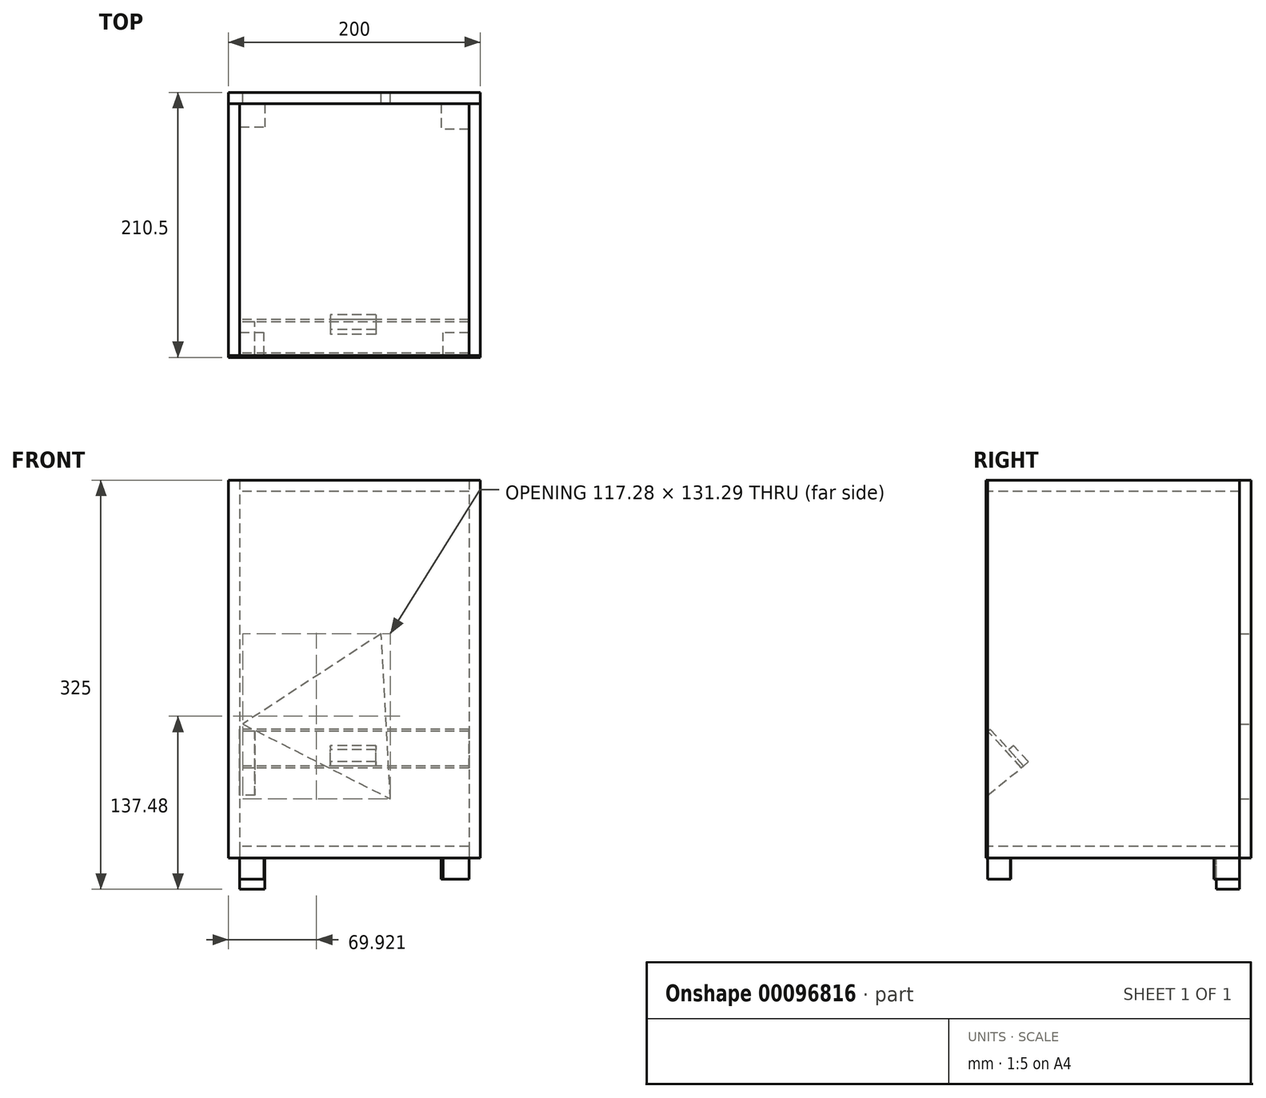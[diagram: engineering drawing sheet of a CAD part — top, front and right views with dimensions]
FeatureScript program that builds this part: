
annotation { "Feature Type Name" : "Feature", "Feature Type Description" : "" }
export const myFeature = defineFeature(function(context is Context, id is Id, definition is map)
    precondition{}
    {
        {
            var Q0;
            Q0=qCreatedBy(makeId("Front.planeOp"),FACE);
            var sketch = newSketch(context, id + "F0", { "sketchPlane" : qUnion([Q0])});
            skLineSegment(sketch, "E0.bottom", {"start": v(0, 0) * mm, "end": v(200, 0) * mm});
            skLineSegment(sketch, "E0.top", {"start": v(0, 300) * mm, "end": v(200, 300) * mm});
            skLineSegment(sketch, "E0.left", {"start": v(0, 0) * mm, "end": v(0, 300) * mm});
            skLineSegment(sketch, "E0.right", {"start": v(200, 0) * mm, "end": v(200, 300) * mm});
            skSolve(sketch);
        }
        {
            var Q0;
            Q0=makeQuery(id+"F0.imprint","IMPRINT",FACE,{"disambiguationData":[TD([[makeQuery(id+"F0.imprint","IMPRINT",EDGE,{"derivedFrom":sQuery(id+"F0.wireOp",EDGE,"E0.bottom")}),1.0]])]});
            extrude(context, id + "F1", {"entities" : qUnion([Q0]), "depth" : 1.5 * mm});
        }
        {
            var Q0;
            Q0=makeQuery(id+"F1.opExtrude","CAP_FACE",FACE,{"disambiguationData":[OSD([sQuery(id+"F0.wireOp",EDGE,"E0.bottom"),sQuery(id+"F0.wireOp",EDGE,"E0.top"),sQuery(id+"F0.wireOp",EDGE,"E0.left"),sQuery(id+"F0.wireOp",EDGE,"E0.right")])],"isStart":true});
            var sketch = newSketch(context, id + "F2", { "sketchPlane" : qUnion([Q0])});
            skLineSegment(sketch, "E1.bottom", {"start": v(0, 300) * mm, "end": v(-9, 300) * mm});
            skLineSegment(sketch, "E1.top", {"start": v(0, 0) * mm, "end": v(-9, 0) * mm});
            skLineSegment(sketch, "E1.left", {"start": v(0, 300) * mm, "end": v(0, 0) * mm});
            skLineSegment(sketch, "E1.right", {"start": v(-9, 300) * mm, "end": v(-9, 0) * mm});
            skSolve(sketch);
        }
        {
            var Q0;
            Q0 = qSketchRegion(id + "F2", true);
            extrude(context, id + "F3", {"entities" : qUnion([Q0]), "depth" : 200 * mm});
        }
        {
            var Q0;
            Q0=makeQuery(id+"F3.opExtrude","SWEPT_FACE",FACE,{"disambiguationData":[OSD([sQuery(id+"F2.wireOp",EDGE,"E1.right")])]});
            var sketch = newSketch(context, id + "F4", { "sketchPlane" : qUnion([Q0])});
            skLineSegment(sketch, "E2", {"start": v(0, 100.67) * mm, "end": v(0, 49.66) * mm});
            skLineSegment(sketch, "E3", {"start": v(0, 49.66) * mm, "end": v(26.79, 71.46) * mm});
            skLineSegment(sketch, "E4", {"start": v(26.79, 71.46) * mm, "end": v(0, 100.67) * mm});
            skSolve(sketch);
        }
        {
            var Q0;
            Q0 = qSketchRegion(id + "F4", true);
            extrude(context, id + "F5", {"entities" : qUnion([Q0]), "depth" : 12 * mm});
        }
        {
            var Q0;
            Q0=makeQuery(id+"F3.opExtrude","SWEPT_FACE",FACE,{"disambiguationData":[OSD([sQuery(id+"F2.wireOp",EDGE,"E1.right")])]});
            var sketch = newSketch(context, id + "F6", { "sketchPlane" : qUnion([Q0])});
            skLineSegment(sketch, "E5", {"start": v(26.7, 71.38) * mm, "end": v(0, 100.68) * mm});
            skLineSegment(sketch, "E6", {"start": v(0, 100.68) * mm, "end": v(1.87, 102.28) * mm});
            skLineSegment(sketch, "E7", {"start": v(1.87, 102.28) * mm, "end": v(28.57, 72.98) * mm});
            skLineSegment(sketch, "E8", {"start": v(28.57, 72.98) * mm, "end": v(26.7, 71.38) * mm});
            skSolve(sketch);
        }
        {
            var Q0;
            Q0 = qSketchRegion(id + "F6", true);
            extrude(context, id + "F7", {"entities" : qUnion([Q0]), "depth" : 182 * mm});
        }
        {
            var Q0;
            Q0=makeQuery(id+"F7.opExtrude","SWEPT_FACE",FACE,{"disambiguationData":[OSD([sQuery(id+"F6.wireOp",EDGE,"E7")])]});
            var sketch = newSketch(context, id + "F8", { "sketchPlane" : qUnion([Q0])});
            skLineSegment(sketch, "E9.bottom", {"start": v(-117.15, 34.7) * mm, "end": v(-80.98, 34.7) * mm});
            skLineSegment(sketch, "E9.top", {"start": v(-117.15, 52.16) * mm, "end": v(-80.98, 52.16) * mm});
            skLineSegment(sketch, "E9.left", {"start": v(-117.15, 34.7) * mm, "end": v(-117.15, 52.16) * mm});
            skLineSegment(sketch, "E9.right", {"start": v(-80.98, 34.7) * mm, "end": v(-80.98, 52.16) * mm});
            skSolve(sketch);
        }
        {
            var Q0;
            Q0 = qSketchRegion(id + "F8", true);
            extrude(context, id + "F9", {"entities" : qUnion([Q0]), "depth" : 5 * mm});
        }
        {
            var Q0;
            Q0=makeQuery(id+"F3.opExtrude","SWEPT_FACE",FACE,{"disambiguationData":[OSD([sQuery(id+"F2.wireOp",EDGE,"E1.right")])]});
            var sketch = newSketch(context, id + "F10", { "sketchPlane" : qUnion([Q0])});
            skLineSegment(sketch, "E10.bottom", {"start": v(200, 300) * mm, "end": v(0, 300) * mm});
            skLineSegment(sketch, "E10.top", {"start": v(200, 291) * mm, "end": v(0, 291) * mm});
            skLineSegment(sketch, "E10.left", {"start": v(200, 300) * mm, "end": v(200, 291) * mm});
            skLineSegment(sketch, "E10.right", {"start": v(0, 300) * mm, "end": v(0, 291) * mm});
            skSolve(sketch);
        }
        {
            var Q0;
            Q0 = qSketchRegion(id + "F10", true);
            extrude(context, id + "F11", {"entities" : qUnion([Q0]), "depth" : 182 * mm});
        }
        {
            var Q0;
            Q0=makeQuery(id+"F3.opExtrude","SWEPT_FACE",FACE,{"disambiguationData":[OSD([sQuery(id+"F2.wireOp",EDGE,"E1.right")])]});
            var sketch = newSketch(context, id + "F12", { "sketchPlane" : qUnion([Q0])});
            skLineSegment(sketch, "E11.bottom", {"start": v(200, 0) * mm, "end": v(0, 0) * mm});
            skLineSegment(sketch, "E11.top", {"start": v(200, 9) * mm, "end": v(0, 9) * mm});
            skLineSegment(sketch, "E11.left", {"start": v(200, 0) * mm, "end": v(200, 9) * mm});
            skLineSegment(sketch, "E11.right", {"start": v(0, 0) * mm, "end": v(0, 9) * mm});
            skSolve(sketch);
        }
        {
            var Q0;
            Q0 = qSketchRegion(id + "F12", true);
            extrude(context, id + "F13", {"entities" : qUnion([Q0]), "depth" : 182 * mm});
        }
        {
            var Q0;
            Q0=makeQuery(id+"F11.opExtrude","CAP_FACE",FACE,{"disambiguationData":[OSD([sQuery(id+"F10.wireOp",EDGE,"E10.bottom"),sQuery(id+"F10.wireOp",EDGE,"E10.top"),sQuery(id+"F10.wireOp",EDGE,"E10.left"),sQuery(id+"F10.wireOp",EDGE,"E10.right")])],"isStart":false});
            var sketch = newSketch(context, id + "F14", { "sketchPlane" : qUnion([Q0])});
            skLineSegment(sketch, "E12.bottom", {"start": v(200, 300) * mm, "end": v(0, 300) * mm});
            skLineSegment(sketch, "E12.top", {"start": v(200, 0) * mm, "end": v(0, 0) * mm});
            skLineSegment(sketch, "E12.left", {"start": v(200, 300) * mm, "end": v(200, 0) * mm});
            skLineSegment(sketch, "E12.right", {"start": v(0, 300) * mm, "end": v(0, 0) * mm});
            skSolve(sketch);
        }
        {
            var Q0;
            Q0 = qSketchRegion(id + "F14", true);
            extrude(context, id + "F15", {"entities" : qUnion([Q0]), "depth" : 9 * mm});
        }
        {
            var Q0;
            Q0=makeQuery(id+"F15.opExtrude","SWEPT_FACE",FACE,{"disambiguationData":[OSD([sQuery(id+"F14.wireOp",EDGE,"E12.left")])]});
            var sketch = newSketch(context, id + "F16", { "sketchPlane" : qUnion([Q0])});
            skLineSegment(sketch, "E13.bottom", {"start": v(-200, 300) * mm, "end": v(0, 300) * mm});
            skLineSegment(sketch, "E13.top", {"start": v(-200, 0) * mm, "end": v(0, 0) * mm});
            skLineSegment(sketch, "E13.left", {"start": v(-200, 300) * mm, "end": v(-200, 0) * mm});
            skLineSegment(sketch, "E13.right", {"start": v(0, 300) * mm, "end": v(0, 0) * mm});
            skSolve(sketch);
        }
        {
            var Q0;
            Q0 = qSketchRegion(id + "F16", true);
            extrude(context, id + "F17", {"entities" : qUnion([Q0]), "depth" : 9 * mm});
        }
        {
            var Q0;
            Q0=makeQuery(id+"F17.opExtrude","CAP_FACE",FACE,{"disambiguationData":[OSD([sQuery(id+"F16.wireOp",EDGE,"E13.bottom"),sQuery(id+"F16.wireOp",EDGE,"E13.top"),sQuery(id+"F16.wireOp",EDGE,"E13.left"),sQuery(id+"F16.wireOp",EDGE,"E13.right")])],"isStart":false});
            var sketch = newSketch(context, id + "F18", { "sketchPlane" : qUnion([Q0])});
            skCircle(sketch, "E14.cCircle", {"center": v(-87.08, 110.41) * mm, "radius": 37.96 * mm, "construction": true});
            skLineSegment(sketch, "E14.0", {"start": v(-11.28, 106.28) * mm, "end": v(-128.56, 46.84) * mm});
            skLineSegment(sketch, "E14.1", {"start": v(-128.56, 46.84) * mm, "end": v(-121.4, 178.13) * mm});
            skLineSegment(sketch, "E14.2", {"start": v(-121.4, 178.13) * mm, "end": v(-11.28, 106.28) * mm});
            skPoint(sketch, "E14.0.midPoint", {"position": v(-69.92, 76.56) * mm});
            skSolve(sketch);
        }
        {
            var Q0;
            Q0 = qSketchRegion(id + "F18", true);
            extrude(context, id + "F19", {"entities" : qUnion([Q0]), "operationType" : NewBodyOperationType.REMOVE, "oppositeDirection" : true, "depth" : 9 * mm});
        }
        {
            var Q0;
            Q0=makeQuery(id+"F13.opExtrude","SWEPT_FACE",FACE,{"disambiguationData":[OSD([sQuery(id+"F12.wireOp",EDGE,"E11.bottom")])]});
            var sketch = newSketch(context, id + "F20", { "sketchPlane" : qUnion([Q0])});
            skLineSegment(sketch, "E15.bottom", {"start": v(9, 0) * mm, "end": v(28.08, 0) * mm});
            skLineSegment(sketch, "E15.top", {"start": v(9, -18.35) * mm, "end": v(28.08, -18.35) * mm});
            skLineSegment(sketch, "E15.left", {"start": v(9, 0) * mm, "end": v(9, -18.35) * mm});
            skLineSegment(sketch, "E15.right", {"start": v(28.08, 0) * mm, "end": v(28.08, -18.35) * mm});
            skSolve(sketch);
        }
        {
            var Q0;
            Q0 = qSketchRegion(id + "F20", true);
            extrude(context, id + "F21", {"entities" : qUnion([Q0]), "depth" : 17 * mm});
        }
        {
            var Q0;
            Q0=makeQuery(id+"F13.opExtrude","SWEPT_FACE",FACE,{"disambiguationData":[OSD([sQuery(id+"F12.wireOp",EDGE,"E11.bottom")])]});
            var sketch = newSketch(context, id + "F22", { "sketchPlane" : qUnion([Q0])});
            skLineSegment(sketch, "E16.bottom", {"start": v(191, 0) * mm, "end": v(170.33, 0) * mm});
            skLineSegment(sketch, "E16.top", {"start": v(191, -18) * mm, "end": v(170.33, -18) * mm});
            skLineSegment(sketch, "E16.left", {"start": v(191, 0) * mm, "end": v(191, -18) * mm});
            skLineSegment(sketch, "E16.right", {"start": v(170.33, 0) * mm, "end": v(170.33, -18) * mm});
            skSolve(sketch);
        }
        {
            var Q0;
            Q0 = qSketchRegion(id + "F22", true);
            extrude(context, id + "F23", {"entities" : qUnion([Q0]), "depth" : 17 * mm});
        }
        {
            var Q0;
            Q0=makeQuery(id+"F13.opExtrude","SWEPT_FACE",FACE,{"disambiguationData":[OSD([sQuery(id+"F12.wireOp",EDGE,"E11.bottom")])]});
            var sketch = newSketch(context, id + "F24", { "sketchPlane" : qUnion([Q0])});
            skLineSegment(sketch, "E17.bottom", {"start": v(9, -200) * mm, "end": v(28.78, -200) * mm});
            skLineSegment(sketch, "E17.top", {"start": v(9, -181.68) * mm, "end": v(28.78, -181.68) * mm});
            skLineSegment(sketch, "E17.left", {"start": v(9, -200) * mm, "end": v(9, -181.68) * mm});
            skLineSegment(sketch, "E17.right", {"start": v(28.78, -200) * mm, "end": v(28.78, -181.68) * mm});
            skSolve(sketch);
        }
        {
            var Q0;
            Q0 = qSketchRegion(id + "F24", true);
            extrude(context, id + "F25", {"entities" : qUnion([Q0]), "depth" : 25 * mm});
        }
        {
            var Q0;
            Q0=makeQuery(id+"F13.opExtrude","SWEPT_FACE",FACE,{"disambiguationData":[OSD([sQuery(id+"F12.wireOp",EDGE,"E11.bottom")])]});
            var sketch = newSketch(context, id + "F26", { "sketchPlane" : qUnion([Q0])});
            skLineSegment(sketch, "E18.bottom", {"start": v(191, -200) * mm, "end": v(168.92, -200) * mm});
            skLineSegment(sketch, "E18.top", {"start": v(191, -179.57) * mm, "end": v(168.92, -179.57) * mm});
            skLineSegment(sketch, "E18.left", {"start": v(191, -200) * mm, "end": v(191, -179.57) * mm});
            skLineSegment(sketch, "E18.right", {"start": v(168.92, -200) * mm, "end": v(168.92, -179.57) * mm});
            skSolve(sketch);
        }
        {
            var Q0;
            Q0 = qSketchRegion(id + "F26", true);
            extrude(context, id + "F27", {"entities" : qUnion([Q0]), "depth" : 17 * mm});
        }
    });
